# Revit family: Sink-All-In-One_Kitchen-KOHLER-Costco-K-78957
name_source: partatom
category: Plumbing Fixtures
units: mm (PartAtom-declared; Revit-internal decimal feet)

## family parameters
Cut with Voids When Loaded = No
Host = Face
OmniClass Number = 23.31.13.00
OmniClass Title = Sinks
Part Type = Normal
Room Calculation Point = No
Round Connector Dimension = Use Diameter
Shared = No

## types (1)
- NA-Stainless
    ADA Compliant = No
    Assembly Code = D2010400
    CW Connection = Yes
    Cold Water Inlet = Cold Water Inlet
    Date Modified = 06/12/2022
    Default Elevation = 36"
    Description = 33 x 22 x 9 Inch Top-Mount/Undermount Single-Bowl Kitchen Sink Kit
    Drain Included = Yes
    Finish = Kohler-Metal-NA-Stainless
    HW Connection = Yes
    Handle Clearance = 3 13/16"
    Height = 11 11/16"
    Hot Water Inlet = Hot Water Inlet
    Length = 33"
    Manufacturer = Kohler Co.
    Master Format 2014 = 22 41 16
    Master Format 2014 Name = Residential Lavatories and Sinks
    Material = Premium 18-Gauge Stainless Steel
    Model = K-78957-1PC-NA
    Product Documentation Link = https://www.us.kohler.com
    Product Name = Costco
    Product Page URL = http://www.us.kohler.com
    Secondary Finish = Kohler-Metal-VS-Vibrant_Stainless
    Spout Reach = 9"
    Type = 1
    URL = https://www.us.kohler.com
    Vent Connection = No
    Waste Connection = Yes
    Waste Water Outlet = Waste Water Outlet
    WaterSense Certified = No
    Width = 22"

## geometry (parser evidence)
native form markers: Sweep x8
no freeform markers — native parametric forms only
